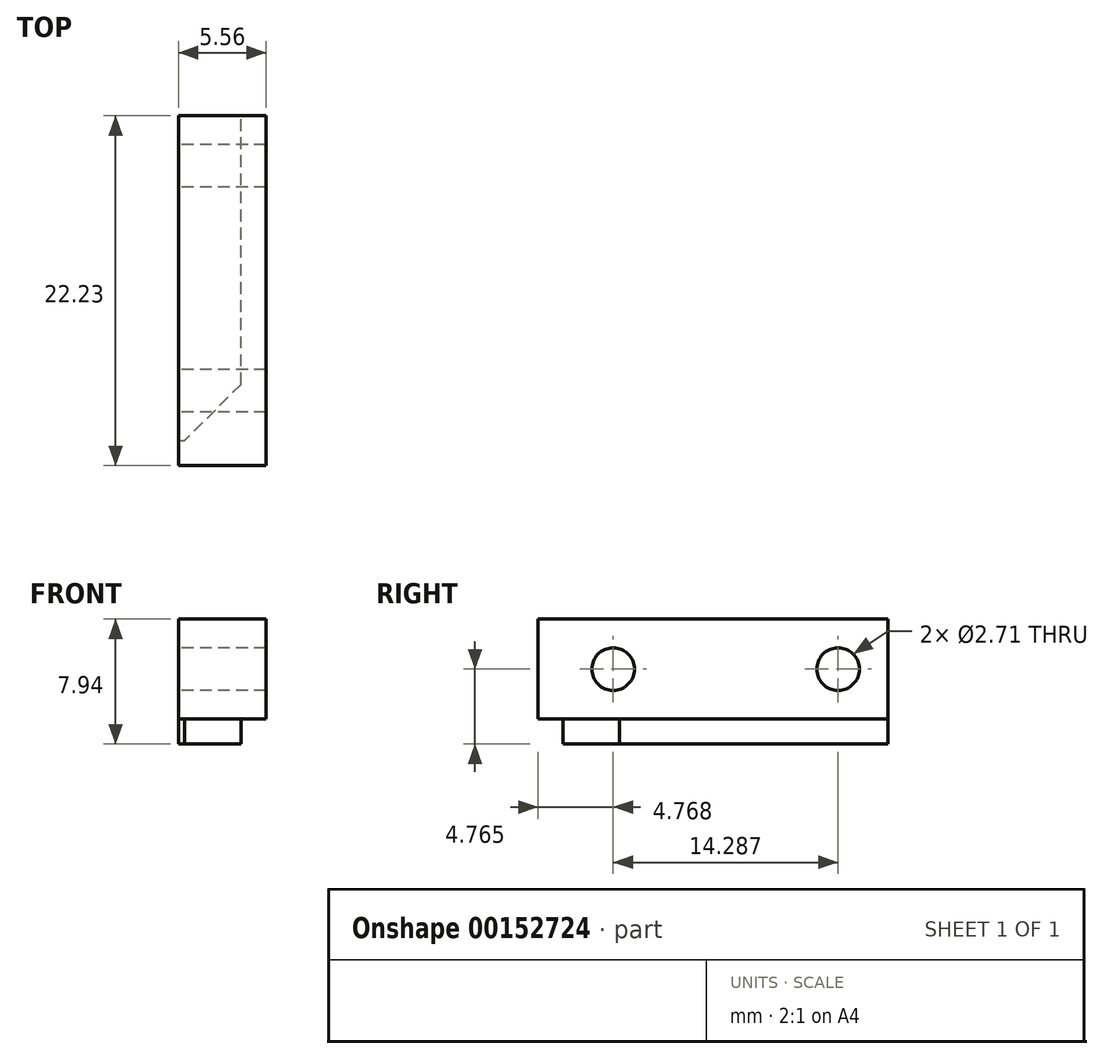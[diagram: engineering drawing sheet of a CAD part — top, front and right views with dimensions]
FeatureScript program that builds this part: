
annotation { "Feature Type Name" : "Feature", "Feature Type Description" : "" }
export const myFeature = defineFeature(function(context is Context, id is Id, definition is map)
    precondition{}
    {
        {
            var Q0;
            Q0=qCreatedBy(makeId("Top.planeOp"),FACE);
            var sketch = newSketch(context, id + "F0", { "sketchPlane" : qUnion([Q0])});
            skLineSegment(sketch, "E0.bottom", {"start": v(0, 0) * mm, "end": v(5.56, 0) * mm});
            skLineSegment(sketch, "E0.top", {"start": v(0, -22.23) * mm, "end": v(5.56, -22.23) * mm});
            skLineSegment(sketch, "E0.left", {"start": v(0, 0) * mm, "end": v(0, -22.23) * mm});
            skLineSegment(sketch, "E0.right", {"start": v(5.56, 0) * mm, "end": v(5.56, -22.23) * mm});
            skSolve(sketch);
        }
        {
            var Q0;
            Q0=qSketchRegion(id+"F0",true);
            extrude(context, id + "F1", {"entities" : qUnion([Q0]), "depth" : 6.35 * mm});
        }
        {
            var Q0;
            Q0=makeQuery(id+"F1.opExtrude","CAP_FACE",FACE,{"disambiguationData":[OSD([sQuery(id+"F0.wireOp",EDGE,"E0.bottom"),sQuery(id+"F0.wireOp",EDGE,"E0.top"),sQuery(id+"F0.wireOp",EDGE,"E0.left"),sQuery(id+"F0.wireOp",EDGE,"E0.right")])],"isStart":true});
            var sketch = newSketch(context, id + "F2", { "sketchPlane" : qUnion([Q0])});
            skLineSegment(sketch, "E1.bottom", {"start": v(0, 0) * mm, "end": v(3.97, 0) * mm});
            skLineSegment(sketch, "E1.top", {"start": v(0, 20.64) * mm, "end": v(3.97, 20.64) * mm});
            skLineSegment(sketch, "E1.left", {"start": v(0, 20.64) * mm, "end": v(0, 0) * mm});
            skLineSegment(sketch, "E1.right", {"start": v(3.97, 20.64) * mm, "end": v(3.97, 0) * mm});
            skLineSegment(sketch, "E2.bottom", {"start": v(3.97, 20.64) * mm, "end": v(5.56, 20.64) * mm, "construction": true});
            skLineSegment(sketch, "E2.top", {"start": v(3.97, 22.23) * mm, "end": v(5.56, 22.23) * mm, "construction": true});
            skLineSegment(sketch, "E2.left", {"start": v(3.97, 22.23) * mm, "end": v(3.97, 20.64) * mm, "construction": true});
            skLineSegment(sketch, "E2.right", {"start": v(5.56, 22.23) * mm, "end": v(5.56, 20.64) * mm, "construction": true});
            skSolve(sketch);
        }
        {
            var Q0;
            Q0=qSketchRegion(id+"F2",true);
            extrude(context, id + "F3", {"entities" : qUnion([Q0]), "operationType" : NewBodyOperationType.ADD, "depth" : 1.59 * mm});
        }
        {
            var Q0;
            Q0=makeQuery(id+"F3.boolean.opBoolean","MERGE",FACE,{"derivedFrom":[makeQuery(id+"F1.opExtrude","SWEPT_FACE",FACE,{"disambiguationData":[OSD([sQuery(id+"F0.wireOp",EDGE,"E0.left")])]}),makeQuery(id+"F3.opExtrude","SWEPT_FACE",FACE,{"disambiguationData":[OSD([sQuery(id+"F2.wireOp",EDGE,"E1.left")])]})]});
            var sketch = newSketch(context, id + "F4", { "sketchPlane" : qUnion([Q0])});
            skLineSegment(sketch, "E3", {"start": v(20.64, 3.18) * mm, "end": v(17.46, 3.18) * mm, "construction": true});
            skLineSegment(sketch, "E4", {"start": v(3.18, 3.18) * mm, "end": v(0, 3.18) * mm, "construction": true});
            skCircle(sketch, "E5", {"center": v(17.46, 3.18) * mm, "radius": 1.35 * mm});
            skCircle(sketch, "E6", {"center": v(3.18, 3.18) * mm, "radius": 1.35 * mm});
            skLineSegment(sketch, "E7", {"start": v(20.64, 0) * mm, "end": v(20.64, 3.18) * mm, "construction": true});
            skSolve(sketch);
        }
        {
            var Q0;
            Q0=qSketchRegion(id+"F4",true);
            extrude(context, id + "F5", {"entities" : qUnion([Q0]), "operationType" : NewBodyOperationType.REMOVE, "oppositeDirection" : true, "depth" : 6.35 * mm});
        }
        {
            var Q0;
            Q0=makeQuery(id+"F3.opExtrude","SWEPT_EDGE",EDGE,{"disambiguationData":[OSD([sQuery(id+"F2.wireOp",EDGE,"E1.top"),sQuery(id+"F2.wireOp",EDGE,"E1.right")])]});
            chamfer(context, id + "F6", {"entities" : qUnion([Q0]), "width" : 3.57 * mm, "tangentPropagation" : true});
        }
    });
